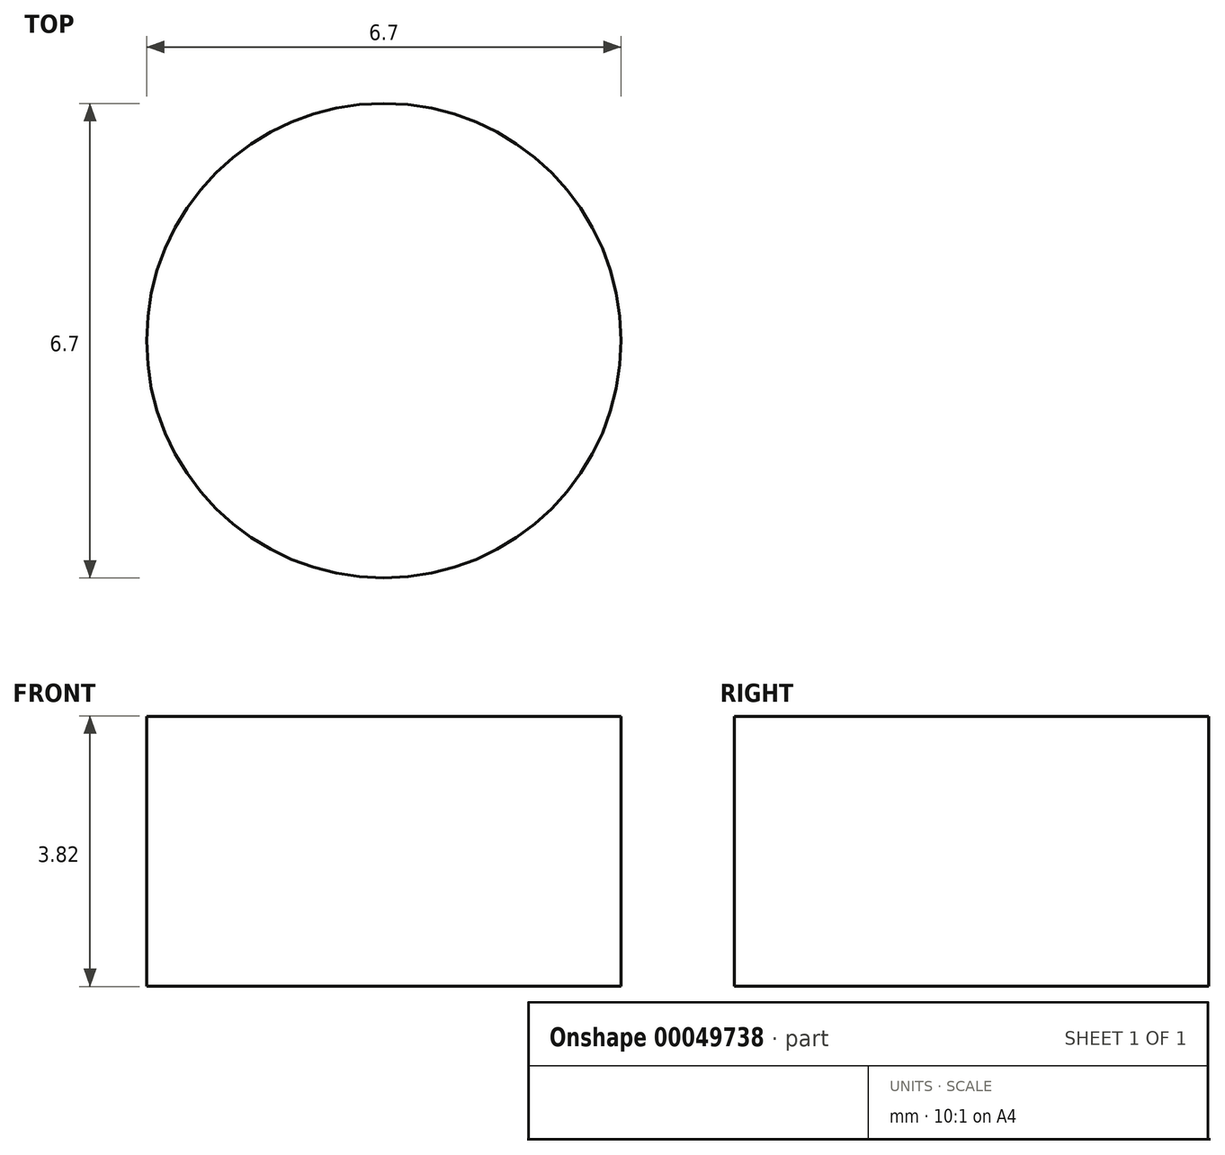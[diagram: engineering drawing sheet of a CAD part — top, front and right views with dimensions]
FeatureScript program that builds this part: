
annotation { "Feature Type Name" : "Feature", "Feature Type Description" : "" }
export const myFeature = defineFeature(function(context is Context, id is Id, definition is map)
    precondition{}
    {
        {
            var Q0;
            Q0=qCreatedBy(makeId("Top.planeOp"),FACE);
            var sketch = newSketch(context, id + "F0", { "sketchPlane" : qUnion([Q0])});
            skCircle(sketch, "E0", {"center": v(0, 0) * mm, "radius": 3.35 * mm});
            skSolve(sketch);
        }
        {
            var Q0;
            Q0=makeQuery(id+"F0.imprint","IMPRINT",FACE,{"disambiguationData":[TD([[makeQuery(id+"F0.imprint","IMPRINT",EDGE,{"derivedFrom":sQuery(id+"F0.wireOp",EDGE,"E0")}),1.0]])]});
            extrude(context, id + "F1", {"entities" : qUnion([Q0]), "depth" : 3.8 * mm, "symmetric" : true});
        }
    });
